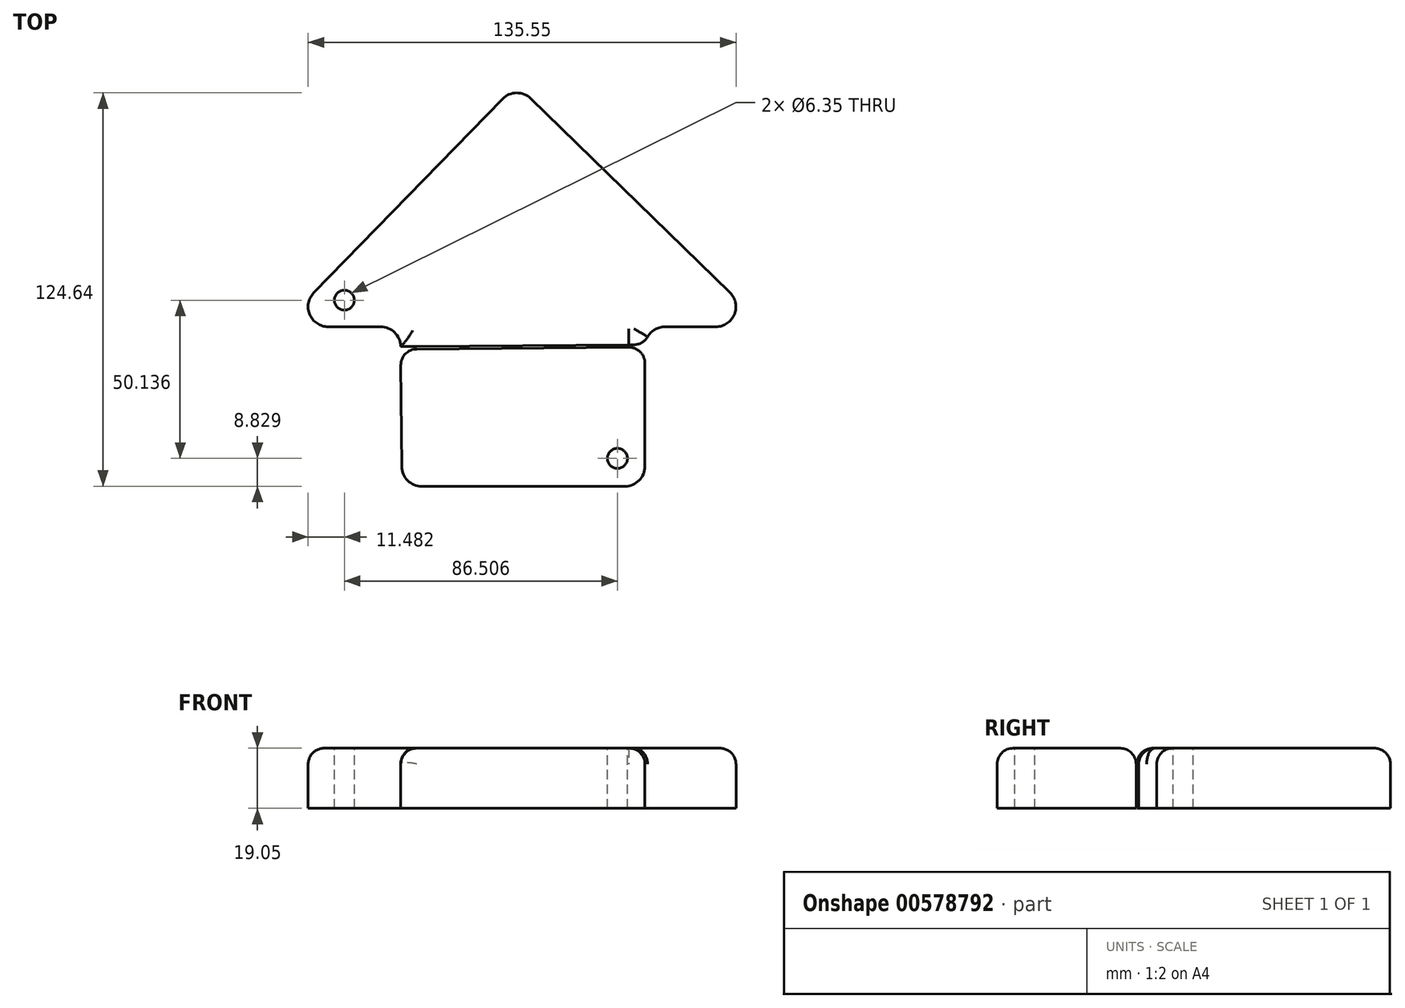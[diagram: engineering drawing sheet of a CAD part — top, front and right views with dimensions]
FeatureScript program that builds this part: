
annotation { "Feature Type Name" : "Feature", "Feature Type Description" : "" }
export const myFeature = defineFeature(function(context is Context, id is Id, definition is map)
    precondition{}
    {
        {
            var Q0;
            Q0=qCreatedBy(makeId("Top.planeOp"),FACE);
            var sketch = newSketch(context, id + "F0", { "sketchPlane" : qUnion([Q0])});
            skLineSegment(sketch, "E0", {"start": v(-2.05, 33.46) * mm, "end": v(14.09, 33.46) * mm});
            skLineSegment(sketch, "E1", {"start": v(18.52, 44.36) * mm, "end": v(-44.55, 105.76) * mm});
            skLineSegment(sketch, "E2", {"start": v(-53.53, 105.64) * mm, "end": v(-113.3, 44.24) * mm});
            skLineSegment(sketch, "E3", {"start": v(-108.76, 33.46) * mm, "end": v(-92.13, 33.46) * mm});
            skLineSegment(sketch, "E4", {"start": v(-14.75, -17.08) * mm, "end": v(-79.11, -17.08) * mm});
            skLineSegment(sketch, "E5", {"start": v(-85.46, -10.78) * mm, "end": v(-85.78, 27.17) * mm});
            skLineSegment(sketch, "E6", {"start": v(-8.4, 27.11) * mm, "end": v(-8.4, -10.73) * mm});
            skPoint(sketch, "E7.visualSharp", {"position": v(29.71, 33.46) * mm});
            skArc(sketch, "E7.filletArc", {"start": v(14.09, 33.46) * mm, "mid": v(19.97, 37.42) * mm, "end": v(18.52, 44.36) * mm});
            skPoint(sketch, "E8.visualSharp", {"position": v(-123.8, 33.46) * mm});
            skArc(sketch, "E8.filletArc", {"start": v(-113.3, 44.24) * mm, "mid": v(-114.6, 37.34) * mm, "end": v(-108.76, 33.46) * mm});
            skPoint(sketch, "E9.visualSharp", {"position": v(-49.1, 110.2) * mm});
            skArc(sketch, "E9.filletArc", {"start": v(-44.55, 105.76) * mm, "mid": v(-49.07, 107.56) * mm, "end": v(-53.53, 105.64) * mm});
            skPoint(sketch, "E10.visualSharp", {"position": v(-85.41, -17.08) * mm});
            skArc(sketch, "E10.filletArc", {"start": v(-85.46, -10.78) * mm, "mid": v(-83.59, -15.24) * mm, "end": v(-79.11, -17.08) * mm});
            skPoint(sketch, "E11.visualSharp", {"position": v(-8.4, -17.08) * mm});
            skArc(sketch, "E11.filletArc", {"start": v(-14.75, -17.08) * mm, "mid": v(-10.26, -15.22) * mm, "end": v(-8.4, -10.73) * mm});
            skPoint(sketch, "E12.visualSharp", {"position": v(-85.83, 33.46) * mm});
            skArc(sketch, "E12.filletArc", {"start": v(-85.78, 27.17) * mm, "mid": v(-87.66, 31.62) * mm, "end": v(-92.13, 33.46) * mm});
            skPoint(sketch, "E13.visualSharp", {"position": v(-8.4, 33.46) * mm});
            skArc(sketch, "E13.filletArc", {"start": v(-2.05, 33.46) * mm, "mid": v(-6.54, 31.6) * mm, "end": v(-8.4, 27.11) * mm});
            skSolve(sketch);
        }
        {
            var Q0;
            Q0=makeQuery(id+"F0.imprint","IMPRINT",FACE,{"disambiguationData":[TD([[makeQuery(id+"F0.imprint","IMPRINT",EDGE,{"derivedFrom":sQuery(id+"F0.wireOp",EDGE,"E0")}),1.0]])]});
            extrude(context, id + "F1", {"entities" : qUnion([Q0]), "depth" : 19.05 * mm, "offsetDistance" : 25.4 * mm});
        }
        {
            var Q0;
            Q0=makeQuery(id+"F1.opExtrude","CAP_FACE",FACE,{"disambiguationData":[OSD([sQuery(id+"F0.wireOp",EDGE,"E0"),sQuery(id+"F0.wireOp",EDGE,"E1"),sQuery(id+"F0.wireOp",EDGE,"E2"),sQuery(id+"F0.wireOp",EDGE,"E3"),sQuery(id+"F0.wireOp",EDGE,"E4"),sQuery(id+"F0.wireOp",EDGE,"E5"),sQuery(id+"F0.wireOp",EDGE,"E6"),sQuery(id+"F0.wireOp",EDGE,"E7.filletArc"),sQuery(id+"F0.wireOp",EDGE,"E8.filletArc"),sQuery(id+"F0.wireOp",EDGE,"E9.filletArc"),sQuery(id+"F0.wireOp",EDGE,"E10.filletArc"),sQuery(id+"F0.wireOp",EDGE,"E11.filletArc"),sQuery(id+"F0.wireOp",EDGE,"E12.filletArc"),sQuery(id+"F0.wireOp",EDGE,"E13.filletArc")])],"isStart":false});
            fillet(context, id + "F2", {"entities" : qUnion([Q0]), "radius" : 5.08 * mm, "tangentPropagation" : true, "allowEdgeOverflow" : false});
        }
        {
            var Q0;
            Q0=makeQuery(id+"F1.opExtrude","CAP_FACE",FACE,{"disambiguationData":[OSD([sQuery(id+"F0.wireOp",EDGE,"E0"),sQuery(id+"F0.wireOp",EDGE,"E1"),sQuery(id+"F0.wireOp",EDGE,"E2"),sQuery(id+"F0.wireOp",EDGE,"E3"),sQuery(id+"F0.wireOp",EDGE,"E4"),sQuery(id+"F0.wireOp",EDGE,"E5"),sQuery(id+"F0.wireOp",EDGE,"E6"),sQuery(id+"F0.wireOp",EDGE,"E7.filletArc"),sQuery(id+"F0.wireOp",EDGE,"E8.filletArc"),sQuery(id+"F0.wireOp",EDGE,"E9.filletArc"),sQuery(id+"F0.wireOp",EDGE,"E10.filletArc"),sQuery(id+"F0.wireOp",EDGE,"E11.filletArc"),sQuery(id+"F0.wireOp",EDGE,"E12.filletArc"),sQuery(id+"F0.wireOp",EDGE,"E13.filletArc")])],"isStart":false});
            var sketch = newSketch(context, id + "F3", { "sketchPlane" : qUnion([Q0])});
            skLineSegment(sketch, "E14", {"start": v(-80.7, 27.2) * mm, "end": v(-13.48, 27.77) * mm});
            skLineSegment(sketch, "E15", {"start": v(-13.48, 27.77) * mm, "end": v(7, 27.77) * mm});
            skLineSegment(sketch, "E16", {"start": v(7, 27.77) * mm, "end": v(7, 27.12) * mm});
            skLineSegment(sketch, "E17", {"start": v(7, 27.12) * mm, "end": v(-92.13, 26.3) * mm});
            skLineSegment(sketch, "E18", {"start": v(-92.13, 26.3) * mm, "end": v(-92.13, 27.2) * mm});
            skLineSegment(sketch, "E19", {"start": v(-92.13, 27.2) * mm, "end": v(-80.7, 27.2) * mm});
            skSolve(sketch);
        }
        {
            var Q0;
            {var subQ1=sQuery(id+"F3.wireOp",EDGE,"E16");Q0=makeQuery(id+"F3.imprint","IMPRINT",FACE,{"disambiguationData":[TD([[makeQuery(id+"F3.imprint","IMPRINT",EDGE,{"derivedFrom":subQ1}),-1.0]])]});}
            var Q1;
            {var subQ0=sQuery(id+"F3.wireOp",EDGE,"E14");Q1=makeQuery(id+"F3.imprint","IMPRINT",FACE,{"disambiguationData":[TD([[makeQuery(id+"F3.imprint","IMPRINT",EDGE,{"derivedFrom":subQ0}),-1.0]])]});}
            var Q2;
            {var subQ0=sQuery(id+"F3.wireOp",EDGE,"E18");Q2=makeQuery(id+"F3.imprint","IMPRINT",FACE,{"disambiguationData":[TD([[makeQuery(id+"F3.imprint","IMPRINT",EDGE,{"derivedFrom":subQ0}),-1.0]])]});}
            extrude(context, id + "F4", {"entities" : qUnion([Q0, Q1, Q2]), "operationType" : NewBodyOperationType.REMOVE, "endBound" : BoundingType.THROUGH_ALL, "oppositeDirection" : true, "depth" : 25.4 * mm, "offsetDistance" : 25.4 * mm});
        }
        {
            var Q0;
            {var subQ0=sQuery(id+"F0.wireOp",EDGE,"E6");var subQ1=sQuery(id+"F0.wireOp",EDGE,"E10.filletArc");var subQ2=sQuery(id+"F0.wireOp",EDGE,"E5");var subQ3=sQuery(id+"F0.wireOp",EDGE,"E4");var subQ4=sQuery(id+"F0.wireOp",EDGE,"E11.filletArc");Q0=makeQuery(id+"F4.boolean.opBoolean","SPLIT",FACE,{"disambiguationData":[TD([makeQuery(id+"F2.opFillet","BLEND_FACE",FACE,{"disambiguationData":[OSD([subQ3])]})])],"derivedFrom":makeQuery(id+"F1.opExtrude","CAP_FACE",FACE,{"disambiguationData":[OSD([sQuery(id+"F0.wireOp",EDGE,"E0"),sQuery(id+"F0.wireOp",EDGE,"E1"),sQuery(id+"F0.wireOp",EDGE,"E2"),sQuery(id+"F0.wireOp",EDGE,"E3"),subQ3,subQ2,subQ0,sQuery(id+"F0.wireOp",EDGE,"E7.filletArc"),sQuery(id+"F0.wireOp",EDGE,"E8.filletArc"),sQuery(id+"F0.wireOp",EDGE,"E9.filletArc"),subQ1,subQ4,sQuery(id+"F0.wireOp",EDGE,"E12.filletArc"),sQuery(id+"F0.wireOp",EDGE,"E13.filletArc")])],"isStart":false})});}
            var Q1;
            {var subQ0=sQuery(id+"F0.wireOp",EDGE,"E9.filletArc");var subQ1=sQuery(id+"F0.wireOp",EDGE,"E8.filletArc");var subQ2=sQuery(id+"F0.wireOp",EDGE,"E7.filletArc");var subQ3=sQuery(id+"F0.wireOp",EDGE,"E0");var subQ4=sQuery(id+"F0.wireOp",EDGE,"E12.filletArc");var subQ5=sQuery(id+"F0.wireOp",EDGE,"E1");var subQ6=sQuery(id+"F0.wireOp",EDGE,"E13.filletArc");var subQ7=sQuery(id+"F0.wireOp",EDGE,"E2");var subQ8=sQuery(id+"F0.wireOp",EDGE,"E3");Q1=makeQuery(id+"F4.boolean.opBoolean","SPLIT",FACE,{"disambiguationData":[TD([makeQuery(id+"F2.opFillet","BLEND_FACE",FACE,{"disambiguationData":[OSD([subQ3])]})])],"derivedFrom":makeQuery(id+"F1.opExtrude","CAP_FACE",FACE,{"disambiguationData":[OSD([subQ3,subQ5,subQ7,subQ8,sQuery(id+"F0.wireOp",EDGE,"E4"),sQuery(id+"F0.wireOp",EDGE,"E5"),sQuery(id+"F0.wireOp",EDGE,"E6"),subQ2,subQ1,subQ0,sQuery(id+"F0.wireOp",EDGE,"E10.filletArc"),sQuery(id+"F0.wireOp",EDGE,"E11.filletArc"),subQ4,subQ6])],"isStart":false})});}
            fillet(context, id + "F5", {"entities" : qUnion([Q0, Q1]), "radius" : 5.08 * mm, "tangentPropagation" : true, "allowEdgeOverflow" : false});
        }
        {
            var Q0;
            {var subQ0=sQuery(id+"F0.wireOp",EDGE,"E9.filletArc");var subQ1=sQuery(id+"F0.wireOp",EDGE,"E8.filletArc");var subQ2=sQuery(id+"F0.wireOp",EDGE,"E7.filletArc");var subQ3=sQuery(id+"F0.wireOp",EDGE,"E0");var subQ4=sQuery(id+"F0.wireOp",EDGE,"E12.filletArc");var subQ5=sQuery(id+"F0.wireOp",EDGE,"E1");var subQ6=sQuery(id+"F0.wireOp",EDGE,"E13.filletArc");var subQ7=sQuery(id+"F0.wireOp",EDGE,"E2");var subQ8=sQuery(id+"F0.wireOp",EDGE,"E3");Q0=makeQuery(id+"F4.boolean.opBoolean","SPLIT",FACE,{"disambiguationData":[TD([makeQuery(id+"F2.opFillet","BLEND_FACE",FACE,{"disambiguationData":[OSD([subQ3])]})])],"derivedFrom":makeQuery(id+"F1.opExtrude","CAP_FACE",FACE,{"disambiguationData":[OSD([subQ3,subQ5,subQ7,subQ8,sQuery(id+"F0.wireOp",EDGE,"E4"),sQuery(id+"F0.wireOp",EDGE,"E5"),sQuery(id+"F0.wireOp",EDGE,"E6"),subQ2,subQ1,subQ0,sQuery(id+"F0.wireOp",EDGE,"E10.filletArc"),sQuery(id+"F0.wireOp",EDGE,"E11.filletArc"),subQ4,subQ6])],"isStart":false})});}
            var sketch = newSketch(context, id + "F6", { "sketchPlane" : qUnion([Q0])});
            skCircle(sketch, "E20", {"center": v(-103.63, 41.89) * mm, "radius": 3.18 * mm});
            skSolve(sketch);
        }
        {
            var Q0;
            Q0=makeQuery(id+"F6.imprint","IMPRINT",FACE,{"disambiguationData":[TD([[makeQuery(id+"F6.imprint","IMPRINT",EDGE,{"derivedFrom":sQuery(id+"F6.wireOp",EDGE,"E20")}),1.0]])]});
            extrude(context, id + "F7", {"entities" : qUnion([Q0]), "operationType" : NewBodyOperationType.REMOVE, "endBound" : BoundingType.THROUGH_ALL, "oppositeDirection" : true, "depth" : 25.4 * mm, "offsetDistance" : 25.4 * mm});
        }
        {
            var Q0;
            {var subQ0=sQuery(id+"F0.wireOp",EDGE,"E6");var subQ1=sQuery(id+"F0.wireOp",EDGE,"E10.filletArc");var subQ2=sQuery(id+"F0.wireOp",EDGE,"E5");var subQ3=sQuery(id+"F0.wireOp",EDGE,"E4");var subQ4=sQuery(id+"F0.wireOp",EDGE,"E11.filletArc");Q0=makeQuery(id+"F4.boolean.opBoolean","SPLIT",FACE,{"disambiguationData":[TD([makeQuery(id+"F2.opFillet","BLEND_FACE",FACE,{"disambiguationData":[OSD([subQ3])]})])],"derivedFrom":makeQuery(id+"F1.opExtrude","CAP_FACE",FACE,{"disambiguationData":[OSD([sQuery(id+"F0.wireOp",EDGE,"E0"),sQuery(id+"F0.wireOp",EDGE,"E1"),sQuery(id+"F0.wireOp",EDGE,"E2"),sQuery(id+"F0.wireOp",EDGE,"E3"),subQ3,subQ2,subQ0,sQuery(id+"F0.wireOp",EDGE,"E7.filletArc"),sQuery(id+"F0.wireOp",EDGE,"E8.filletArc"),sQuery(id+"F0.wireOp",EDGE,"E9.filletArc"),subQ1,subQ4,sQuery(id+"F0.wireOp",EDGE,"E12.filletArc"),sQuery(id+"F0.wireOp",EDGE,"E13.filletArc")])],"isStart":false})});}
            var sketch = newSketch(context, id + "F8", { "sketchPlane" : qUnion([Q0])});
            skCircle(sketch, "E21", {"center": v(-17.12, -8.25) * mm, "radius": 3.18 * mm});
            skSolve(sketch);
        }
        {
            var Q0;
            Q0 = qSketchRegion(id + "F8", true);
            extrude(context, id + "F9", {"entities" : qUnion([Q0]), "operationType" : NewBodyOperationType.REMOVE, "endBound" : BoundingType.THROUGH_ALL, "oppositeDirection" : true, "depth" : 25.4 * mm, "offsetDistance" : 25.4 * mm});
        }
    });
